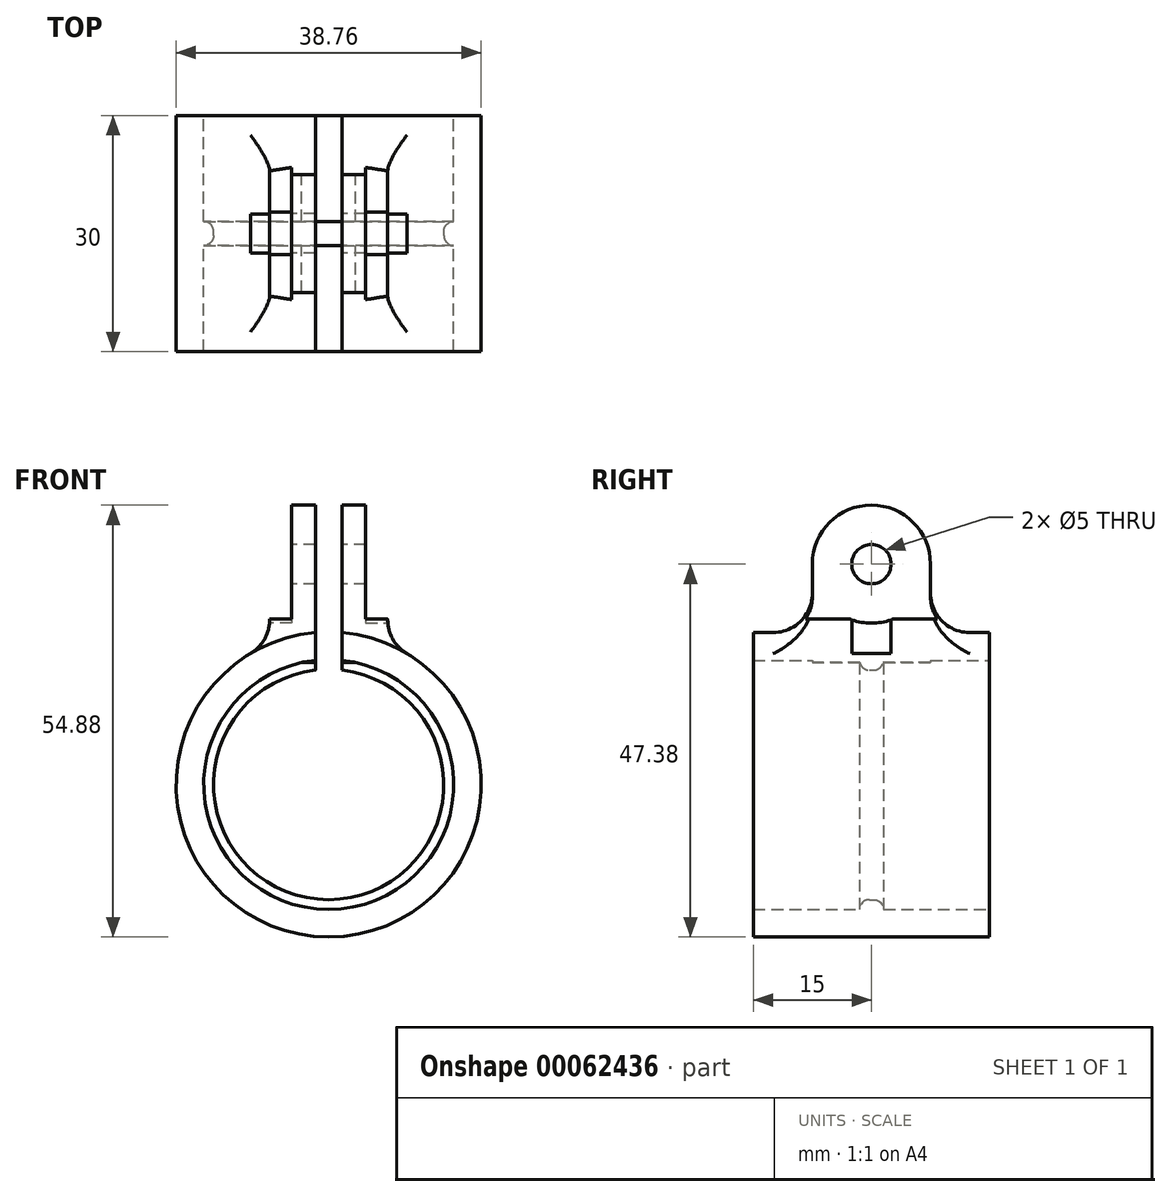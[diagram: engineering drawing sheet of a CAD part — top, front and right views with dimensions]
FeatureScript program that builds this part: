
annotation { "Feature Type Name" : "Feature", "Feature Type Description" : "" }
export const myFeature = defineFeature(function(context is Context, id is Id, definition is map)
    precondition{}
    {
        {
            var Q0;
            Q0=qCreatedBy(makeId("Right.planeOp"),FACE);
            var sketch = newSketch(context, id + "F0", { "sketchPlane" : qUnion([Q0])});
            skArc(sketch, "E0", {"start": v(7.5, 0) * mm, "mid": v(0, 7.5) * mm, "end": v(-7.5, 0) * mm});
            skCircle(sketch, "E1", {"center": v(0, 0) * mm, "radius": 2.5 * mm});
            skLineSegment(sketch, "E2", {"start": v(-7.5, 0) * mm, "end": v(-7.5, -12.5) * mm});
            skLineSegment(sketch, "E3", {"start": v(7.5, 0) * mm, "end": v(7.5, -12.5) * mm});
            skLineSegment(sketch, "E4", {"start": v(7.5, -12.5) * mm, "end": v(-7.5, -12.5) * mm});
            skSolve(sketch);
        }
        {
            var Q0;
            Q0=makeQuery(id+"F0.imprint","IMPRINT",FACE,{"disambiguationData":[TD([[makeQuery(id+"F0.imprint","IMPRINT",EDGE,{"derivedFrom":sQuery(id+"F0.wireOp",EDGE,"E0")}),1.0]])]});
            extrude(context, id + "F1", {"entities" : qUnion([Q0]), "endBound" : BoundingType.SYMMETRIC, "depth" : 15 * mm});
        }
        {
            var Q0;
            Q0=qCreatedBy(makeId("Front.planeOp"),FACE);
            var sketch = newSketch(context, id + "F2", { "sketchPlane" : qUnion([Q0])});
            skLineSegment(sketch, "E5", {"start": v(0, -18.95) * mm, "end": v(0, 19.26) * mm, "construction": true});
            skLineSegment(sketch, "E6", {"start": v(-12.45, 0) * mm, "end": v(16.05, 0) * mm, "construction": true});
            skLineSegment(sketch, "E7.0", {"start": v(-1.7, -7) * mm, "end": v(-1.7, 8.45) * mm});
            skLineSegment(sketch, "E8.0.MirrorCS", {"start": v(1.7, -7) * mm, "end": v(1.7, 8.45) * mm});
            skLineSegment(sketch, "E9.0", {"start": v(-8.58, -7) * mm, "end": v(-4.7, -7) * mm});
            skLineSegment(sketch, "E10.0", {"start": v(4.7, -7) * mm, "end": v(4.7, 8.45) * mm});
            skLineSegment(sketch, "E11.0", {"start": v(-4.7, -7) * mm, "end": v(-4.7, 8.45) * mm});
            skPoint(sketch, "E12.orphan", {"position": v(-1.7, -18.95) * mm});
            skLineSegment(sketch, "E13.trimOffspring", {"start": v(4.7, -7) * mm, "end": v(8.53, -7) * mm});
            skPoint(sketch, "E14.orphan", {"position": v(1.7, -18.95) * mm});
            skLineSegment(sketch, "E15", {"start": v(-8.58, 8.45) * mm, "end": v(-4.7, 8.45) * mm});
            skLineSegment(sketch, "E16", {"start": v(8.53, 8.45) * mm, "end": v(8.53, -7) * mm});
            skLineSegment(sketch, "E17", {"start": v(-8.58, -7) * mm, "end": v(-8.58, 8.45) * mm});
            skLineSegment(sketch, "E18.trimOffspring", {"start": v(-1.7, 8.45) * mm, "end": v(1.7, 8.45) * mm});
            skPoint(sketch, "E19.orphan", {"position": v(-1.7, 19.26) * mm});
            skPoint(sketch, "E20.orphan", {"position": v(1.7, 19.26) * mm});
            skLineSegment(sketch, "E21.trimOffspring", {"start": v(4.7, 8.45) * mm, "end": v(8.53, 8.45) * mm});
            skLineSegment(sketch, "E22", {"start": v(1.7, -7) * mm, "end": v(-1.7, -7) * mm});
            skSolve(sketch);
        }
        {
            var Q0;
            {Q0=qUnion([makeQuery(id+"F2.imprint","IMPRINT",FACE,{"disambiguationData":[TD([[makeQuery(id+"F2.imprint","IMPRINT",EDGE,{"derivedFrom":sQuery(id+"F2.wireOp",EDGE,"E7.0")}),-1.0]])]}),makeQuery(id+"F2.imprint","IMPRINT",FACE,{"disambiguationData":[TD([[makeQuery(id+"F2.imprint","IMPRINT",EDGE,{"derivedFrom":sQuery(id+"F2.wireOp",EDGE,"E9.0")}),1.0]])]}),makeQuery(id+"F2.imprint","IMPRINT",FACE,{"disambiguationData":[TD([[makeQuery(id+"F2.imprint","IMPRINT",EDGE,{"derivedFrom":sQuery(id+"F2.wireOp",EDGE,"E10.0")}),-1.0]])]})]);}
            extrude(context, id + "F3", {"entities" : qUnion([Q0]), "operationType" : NewBodyOperationType.REMOVE, "endBound" : BoundingType.SYMMETRIC, "oppositeDirection" : true, "depth" : 32.83 * mm});
        }
        {
            var Q0;
            Q0=makeQuery(id+"F1.opExtrude","CAP_FACE",FACE,{"disambiguationData":[OSD([sQuery(id+"F0.wireOp",EDGE,"E0"),sQuery(id+"F0.wireOp",EDGE,"E1"),sQuery(id+"F0.wireOp",EDGE,"E2"),sQuery(id+"F0.wireOp",EDGE,"E3"),sQuery(id+"F0.wireOp",EDGE,"E4")])],"isStart":true});
            var sketch = newSketch(context, id + "F4", { "sketchPlane" : qUnion([Q0])});
            skCircle(sketch, "E23", {"center": v(0, 0) * mm, "radius": 7.5 * mm});
            skSolve(sketch);
        }
        {
            var Q0;
            {var subQ0=makeQuery(id+"F3.boolean.opBoolean","INTERSECT",EDGE,{"derivedFrom":[makeQuery(id+"F1.opExtrude","CAP_FACE",FACE,{"disambiguationData":[OSD([sQuery(id+"F0.wireOp",EDGE,"E0"),sQuery(id+"F0.wireOp",EDGE,"E1"),sQuery(id+"F0.wireOp",EDGE,"E2"),sQuery(id+"F0.wireOp",EDGE,"E3"),sQuery(id+"F0.wireOp",EDGE,"E4")])],"isStart":true}),makeQuery(id+"F3.opExtrude","SWEPT_FACE",FACE,{"disambiguationData":[OSD([sQuery(id+"F2.wireOp",EDGE,"E9.0")])]})]});var subQ1=sQuery(id+"F4.wireOp",EDGE,"E23");var subQ3=makeQuery(id+"F4.imprint","INTERSECT",VERTEX,{"disambiguationData":[OD(0.0)],"derivedFrom":[subQ0,subQ1]});Q0=qUnion([makeQuery(id+"F4.imprint","IMPRINT",FACE,{"disambiguationData":[TD([[makeQuery(id+"F4.imprint","IMPRINT",EDGE,{"disambiguationData":[TD([[subQ3,-1.0]])],"derivedFrom":subQ1}),1.0]])]}),makeQuery(id+"F4.imprint","IMPRINT",FACE,{"disambiguationData":[TD([[makeQuery(id+"F4.imprint","IMPRINT",EDGE,{"disambiguationData":[TD([[subQ3,1.0]])],"derivedFrom":subQ1}),1.0]])]})]);}
            var Q1;
            Q1=makeQuery(id+"F3.boolean.opBoolean","COPY",FACE,{"derivedFrom":makeQuery(id+"F3.opExtrude","SWEPT_FACE",FACE,{"disambiguationData":[OSD([sQuery(id+"F2.wireOp",EDGE,"E11.0")])]})});
            extrude(context, id + "F5", {"entities" : qUnion([Q0]), "operationType" : NewBodyOperationType.REMOVE, "endBound" : BoundingType.UP_TO_SURFACE, "oppositeDirection" : true, "endBoundEntityFace" : qUnion([Q1]), "depth" : 25 * mm});
        }
        {
            var Q0;
            Q0=makeQuery(id+"F1.opExtrude","CAP_FACE",FACE,{"disambiguationData":[OSD([sQuery(id+"F0.wireOp",EDGE,"E0"),sQuery(id+"F0.wireOp",EDGE,"E1"),sQuery(id+"F0.wireOp",EDGE,"E2"),sQuery(id+"F0.wireOp",EDGE,"E3"),sQuery(id+"F0.wireOp",EDGE,"E4")])],"isStart":false});
            var sketch = newSketch(context, id + "F6", { "sketchPlane" : qUnion([Q0])});
            skCircle(sketch, "E24", {"center": v(0, 0) * mm, "radius": 7.5 * mm});
            skSolve(sketch);
        }
        {
            var Q0;
            {var subQ0=makeQuery(id+"F3.boolean.opBoolean","INTERSECT",EDGE,{"derivedFrom":[makeQuery(id+"F1.opExtrude","CAP_FACE",FACE,{"disambiguationData":[OSD([sQuery(id+"F0.wireOp",EDGE,"E0"),sQuery(id+"F0.wireOp",EDGE,"E1"),sQuery(id+"F0.wireOp",EDGE,"E2"),sQuery(id+"F0.wireOp",EDGE,"E3"),sQuery(id+"F0.wireOp",EDGE,"E4")])],"isStart":false}),makeQuery(id+"F3.opExtrude","SWEPT_FACE",FACE,{"disambiguationData":[OSD([sQuery(id+"F2.wireOp",EDGE,"E13.trimOffspring")])]})]});var subQ1=sQuery(id+"F6.wireOp",EDGE,"E24");var subQ3=makeQuery(id+"F6.imprint","INTERSECT",VERTEX,{"disambiguationData":[OD(0.0)],"derivedFrom":[subQ0,subQ1]});Q0=qUnion([makeQuery(id+"F6.imprint","IMPRINT",FACE,{"disambiguationData":[TD([[makeQuery(id+"F6.imprint","IMPRINT",EDGE,{"disambiguationData":[TD([[subQ3,1.0]])],"derivedFrom":subQ1}),1.0]])]}),makeQuery(id+"F6.imprint","IMPRINT",FACE,{"disambiguationData":[TD([[makeQuery(id+"F6.imprint","IMPRINT",EDGE,{"disambiguationData":[TD([[subQ3,-1.0]])],"derivedFrom":subQ1}),1.0]])]})]);}
            var Q1;
            Q1=makeQuery(id+"F3.boolean.opBoolean","COPY",FACE,{"derivedFrom":makeQuery(id+"F3.opExtrude","SWEPT_FACE",FACE,{"disambiguationData":[OSD([sQuery(id+"F2.wireOp",EDGE,"E10.0")])]})});
            extrude(context, id + "F7", {"entities" : qUnion([Q0]), "operationType" : NewBodyOperationType.REMOVE, "endBound" : BoundingType.UP_TO_SURFACE, "oppositeDirection" : true, "endBoundEntityFace" : qUnion([Q1]), "depth" : 25 * mm});
        }
        {
            var Q0;
            Q0=qCreatedBy(makeId("Front.planeOp"),FACE);
            var sketch = newSketch(context, id + "F8", { "sketchPlane" : qUnion([Q0])});
            skLineSegment(sketch, "E25", {"start": v(0, 0) * mm, "end": v(0, -28) * mm});
            skCircle(sketch, "E26", {"center": v(0, -28) * mm, "radius": 19.38 * mm});
            skCircle(sketch, "E27", {"center": v(0, -28) * mm, "radius": 15.88 * mm});
            skCircle(sketch, "E28", {"center": v(0, -28) * mm, "radius": 14.62 * mm});
            skSolve(sketch);
        }
        {
            var Q0;
            Q0=makeQuery(id+"F8.imprint","IMPRINT",FACE,{"disambiguationData":[TD([[makeQuery(id+"F8.imprint","IMPRINT",EDGE,{"derivedFrom":sQuery(id+"F8.wireOp",EDGE,"E26")}),1.0]])]});
            extrude(context, id + "F9", {"entities" : qUnion([Q0]), "operationType" : NewBodyOperationType.ADD, "depth" : 15 * mm, "hasSecondDirection" : true, "secondDirectionOppositeDirection" : true, "secondDirectionDepth" : 15 * mm});
        }
        {
            var Q0;
            Q0=makeQuery(id+"F8.imprint","IMPRINT",FACE,{"disambiguationData":[TD([[makeQuery(id+"F8.imprint","IMPRINT",EDGE,{"derivedFrom":sQuery(id+"F8.wireOp",EDGE,"E27")}),1.0]])]});
            extrude(context, id + "F10", {"entities" : qUnion([Q0]), "operationType" : NewBodyOperationType.ADD, "depth" : 1.52 * mm, "hasSecondDirection" : true, "secondDirectionOppositeDirection" : true, "secondDirectionDepth" : 1.52 * mm});
        }
        {
            var Q0;
            Q0=makeQuery(id+"F9.boolean.opBoolean","INTERSECT",EDGE,{"derivedFrom":[makeQuery(id+"F1.opExtrude","SWEPT_FACE",FACE,{"disambiguationData":[OSD([sQuery(id+"F0.wireOp",EDGE,"E3")])]}),makeQuery(id+"F9.opExtrude","SWEPT_FACE",FACE,{"disambiguationData":[OSD([sQuery(id+"F8.wireOp",EDGE,"E26")])]})]});
            var Q1;
            Q1=makeQuery(id+"F9.boolean.opBoolean","INTERSECT",EDGE,{"derivedFrom":[makeQuery(id+"F1.opExtrude","CAP_FACE",FACE,{"disambiguationData":[OSD([sQuery(id+"F0.wireOp",EDGE,"E0"),sQuery(id+"F0.wireOp",EDGE,"E1"),sQuery(id+"F0.wireOp",EDGE,"E2"),sQuery(id+"F0.wireOp",EDGE,"E3"),sQuery(id+"F0.wireOp",EDGE,"E4")])],"isStart":false}),makeQuery(id+"F9.opExtrude","SWEPT_FACE",FACE,{"disambiguationData":[OSD([sQuery(id+"F8.wireOp",EDGE,"E26")])]})]});
            var Q2;
            Q2=makeQuery(id+"F9.boolean.opBoolean","INTERSECT",EDGE,{"derivedFrom":[makeQuery(id+"F1.opExtrude","CAP_FACE",FACE,{"disambiguationData":[OSD([sQuery(id+"F0.wireOp",EDGE,"E0"),sQuery(id+"F0.wireOp",EDGE,"E1"),sQuery(id+"F0.wireOp",EDGE,"E2"),sQuery(id+"F0.wireOp",EDGE,"E3"),sQuery(id+"F0.wireOp",EDGE,"E4")])],"isStart":true}),makeQuery(id+"F9.opExtrude","SWEPT_FACE",FACE,{"disambiguationData":[OSD([sQuery(id+"F8.wireOp",EDGE,"E26")])]})]});
            var Q3;
            Q3=makeQuery(id+"F9.boolean.opBoolean","INTERSECT",EDGE,{"derivedFrom":[makeQuery(id+"F1.opExtrude","SWEPT_FACE",FACE,{"disambiguationData":[OSD([sQuery(id+"F0.wireOp",EDGE,"E2")])]}),makeQuery(id+"F9.opExtrude","SWEPT_FACE",FACE,{"disambiguationData":[OSD([sQuery(id+"F8.wireOp",EDGE,"E26")])]})]});
            fillet(context, id + "F11", {"entities" : qUnion([Q0, Q1, Q2, Q3]), "radius" : 5 * mm, "tangentPropagation" : true, "allowEdgeOverflow" : false});
        }
        {
            var Q0;
            Q0=qCreatedBy(makeId("Front.planeOp"),FACE);
            var sketch = newSketch(context, id + "F12", { "sketchPlane" : qUnion([Q0])});
            skLineSegment(sketch, "E29.rect.bottom", {"start": v(-1.7, -36.47) * mm, "end": v(1.7, -36.47) * mm});
            skLineSegment(sketch, "E29.rect.top", {"start": v(-1.7, 36.47) * mm, "end": v(1.7, 36.47) * mm});
            skLineSegment(sketch, "E29.rect.left", {"start": v(-1.7, -36.47) * mm, "end": v(-1.7, 36.47) * mm});
            skLineSegment(sketch, "E29.rect.right", {"start": v(1.7, -36.47) * mm, "end": v(1.7, 36.47) * mm});
            skPoint(sketch, "E29.rect.middle", {"position": v(0, 0) * mm});
            skSolve(sketch);
        }
        {
            var Q0;
            Q0=makeQuery(id+"F12.imprint","IMPRINT",FACE,{"disambiguationData":[TD([[makeQuery(id+"F12.imprint","IMPRINT",EDGE,{"derivedFrom":sQuery(id+"F12.wireOp",EDGE,"E29.rect.bottom")}),1.0]])]});
            extrude(context, id + "F13", {"entities" : qUnion([Q0]), "operationType" : NewBodyOperationType.REMOVE, "oppositeDirection" : true, "depth" : 25 * mm, "hasSecondDirection" : true, "secondDirectionOppositeDirection" : false, "secondDirectionDepth" : 25 * mm});
        }
        {
            var Q0;
            Q0=makeQuery(id+"F10.opExtrude","CAP_EDGE",EDGE,{"disambiguationData":[OSD([sQuery(id+"F8.wireOp",EDGE,"E28")])],"isStart":false});
            var Q1;
            Q1=makeQuery(id+"F10.opExtrude","CAP_EDGE",EDGE,{"disambiguationData":[OSD([sQuery(id+"F8.wireOp",EDGE,"E28")])],"isStart":true});
            fillet(context, id + "F14", {"entities" : qUnion([Q0, Q1]), "radius" : 1.25 * mm, "tangentPropagation" : true, "allowEdgeOverflow" : false});
        }
    });
